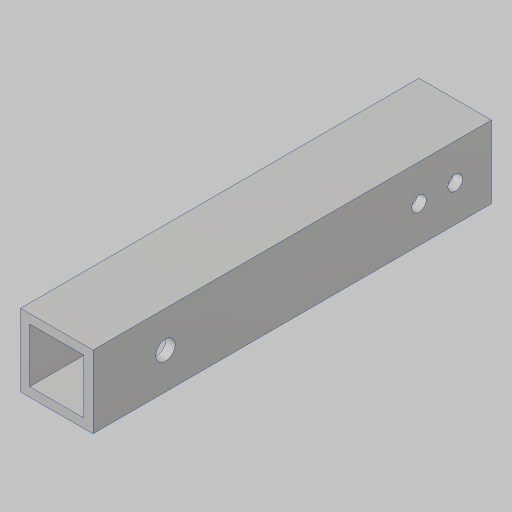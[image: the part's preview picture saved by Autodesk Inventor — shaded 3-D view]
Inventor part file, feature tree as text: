
AUTODESK INVENTOR PART (.ipt)
format: ipt  version: 2023.5 (Build 275446000, 446)  size: 119,808 bytes
history: native  units: in
note: dims shown in document units (in); Inventor stores cm internally (conversion verified against a paired STEP export)
features: hole x2, sketch x2, extrude x1
ambient origin geometry x8: Origin, YZ Plane, XZ Plane, XY Plane, X Axis, Y Axis, Z Axis, Center Point
bodies: Solid1 (feature_tree)
feature tree (5):
  extrude  "Extrusion1"  Depth=1.0in
  hole  "Hole1"  [1 undecoded]
  hole  "Hole2"  [1 undecoded]
  sketch  "Sketch2"  dims[d4=0.0in d5=1.0in]
  sketch  "Sketch3"  dims[d6=0.266in d7=0.75in d8=0.507in d9=0.25in d10=0.5635in d11=1.0in d12=0.8108in d13=0.5in d14=0.5in d15=0.201in d16=0.75in d17=0.385in d18=0.25in d19=0.5635in d20=1.0in d21=0.8108in]
note: 2 required parameter values undecoded (feature->parameter linkage not recoverable at this tier; creation-order binding heuristic only, values carry confidence <= 0.55)
